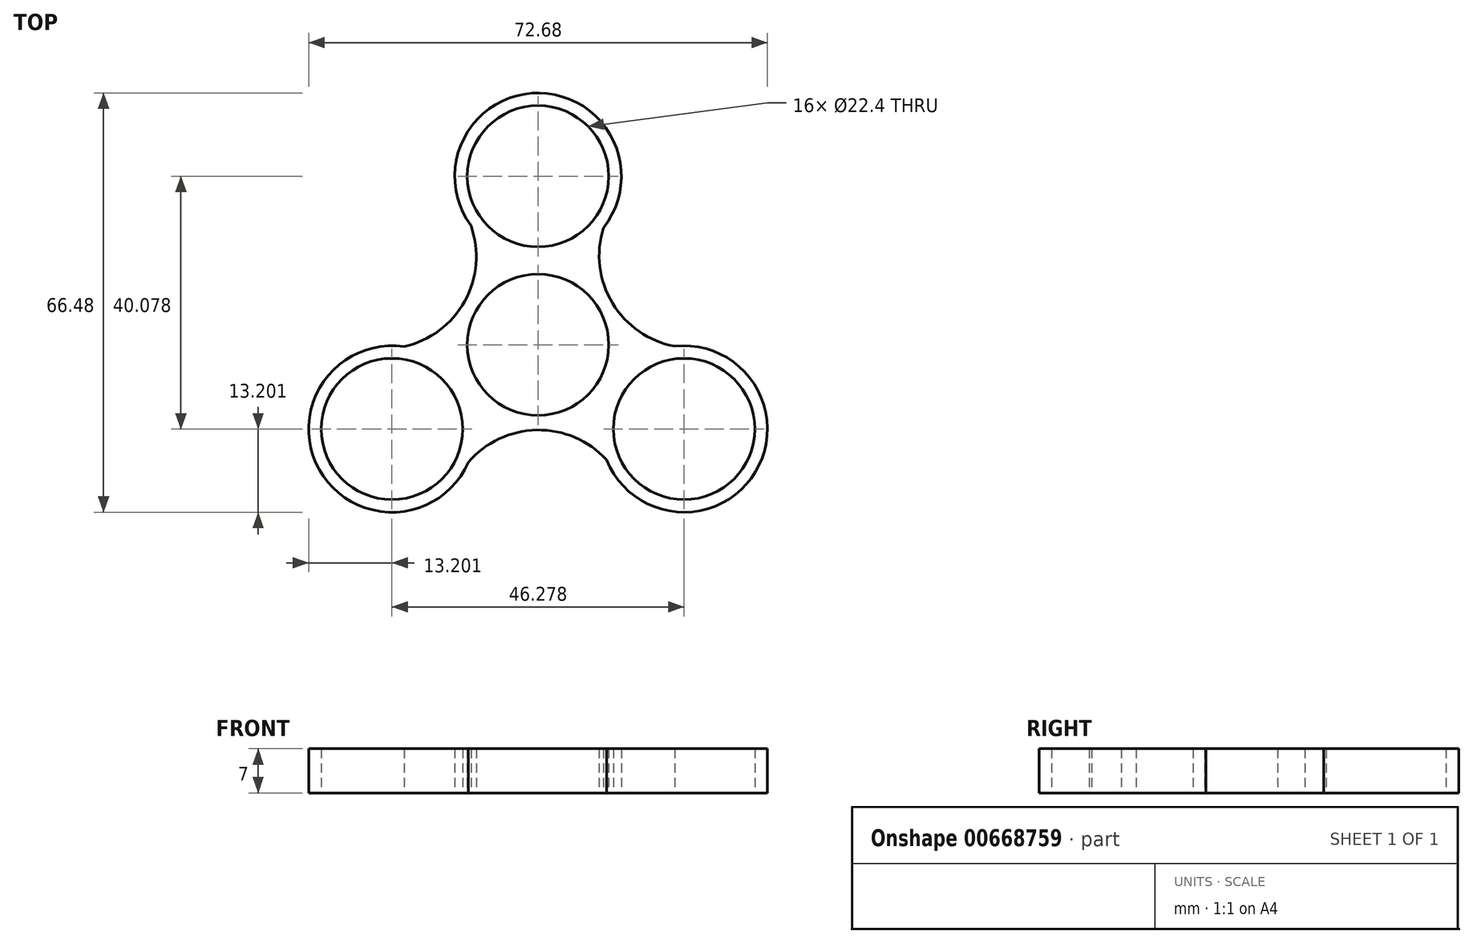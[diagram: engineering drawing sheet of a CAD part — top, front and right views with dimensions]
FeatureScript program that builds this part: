
annotation { "Feature Type Name" : "Feature", "Feature Type Description" : "" }
export const myFeature = defineFeature(function(context is Context, id is Id, definition is map)
    precondition{}
    {
        {
            var Q0;
            Q0=qCreatedBy(makeId("Top.planeOp"),FACE);
            var sketch = newSketch(context, id + "F0", { "sketchPlane" : qUnion([Q0])});
            skCircle(sketch, "E0", {"center": v(0, 0) * mm, "radius": 11.2 * mm});
            skCircle(sketch, "E1", {"center": v(0, 26.72) * mm, "radius": 11.2 * mm});
            skArc(sketch, "E2", {"start": v(10.35, 18.53) * mm, "mid": v(0.22, 39.92) * mm, "end": v(-10.63, 18.89) * mm});
            skCircle(sketch, "E3.1.0", {"center": v(-23.14, -13.36) * mm, "radius": 11.2 * mm});
            skArc(sketch, "E3.1.1", {"start": v(-21.23, -0.3) * mm, "mid": v(-34.68, -19.76) * mm, "end": v(-11.04, -18.65) * mm});
            skCircle(sketch, "E3.2.0", {"center": v(23.14, -13.36) * mm, "radius": 11.2 * mm});
            skArc(sketch, "E3.2.1", {"start": v(10.87, -18.23) * mm, "mid": v(34.46, -20.15) * mm, "end": v(21.67, -0.24) * mm});
            skArc(sketch, "E4", {"start": v(10.35, 18.53) * mm, "mid": v(11.8, 6.6) * mm, "end": v(21.67, -0.24) * mm});
            skArc(sketch, "E5.1.0", {"start": v(-21.23, -0.3) * mm, "mid": v(-11.62, 6.91) * mm, "end": v(-10.63, 18.89) * mm});
            skArc(sketch, "E5.2.0", {"start": v(10.87, -18.23) * mm, "mid": v(-0.18, -13.52) * mm, "end": v(-11.04, -18.65) * mm});
            skSolve(sketch);
        }
        {
            var Q0;
            Q0=makeQuery(id+"F0.imprint","IMPRINT",FACE,{"disambiguationData":[TD([[makeQuery(id+"F0.imprint","IMPRINT",EDGE,{"derivedFrom":sQuery(id+"F0.wireOp",EDGE,"E0")}),-1.0]])]});
            extrude(context, id + "F1", {"entities" : qUnion([Q0]), "depth" : 7 * mm, "offsetDistance" : 25 * mm});
        }
    });
